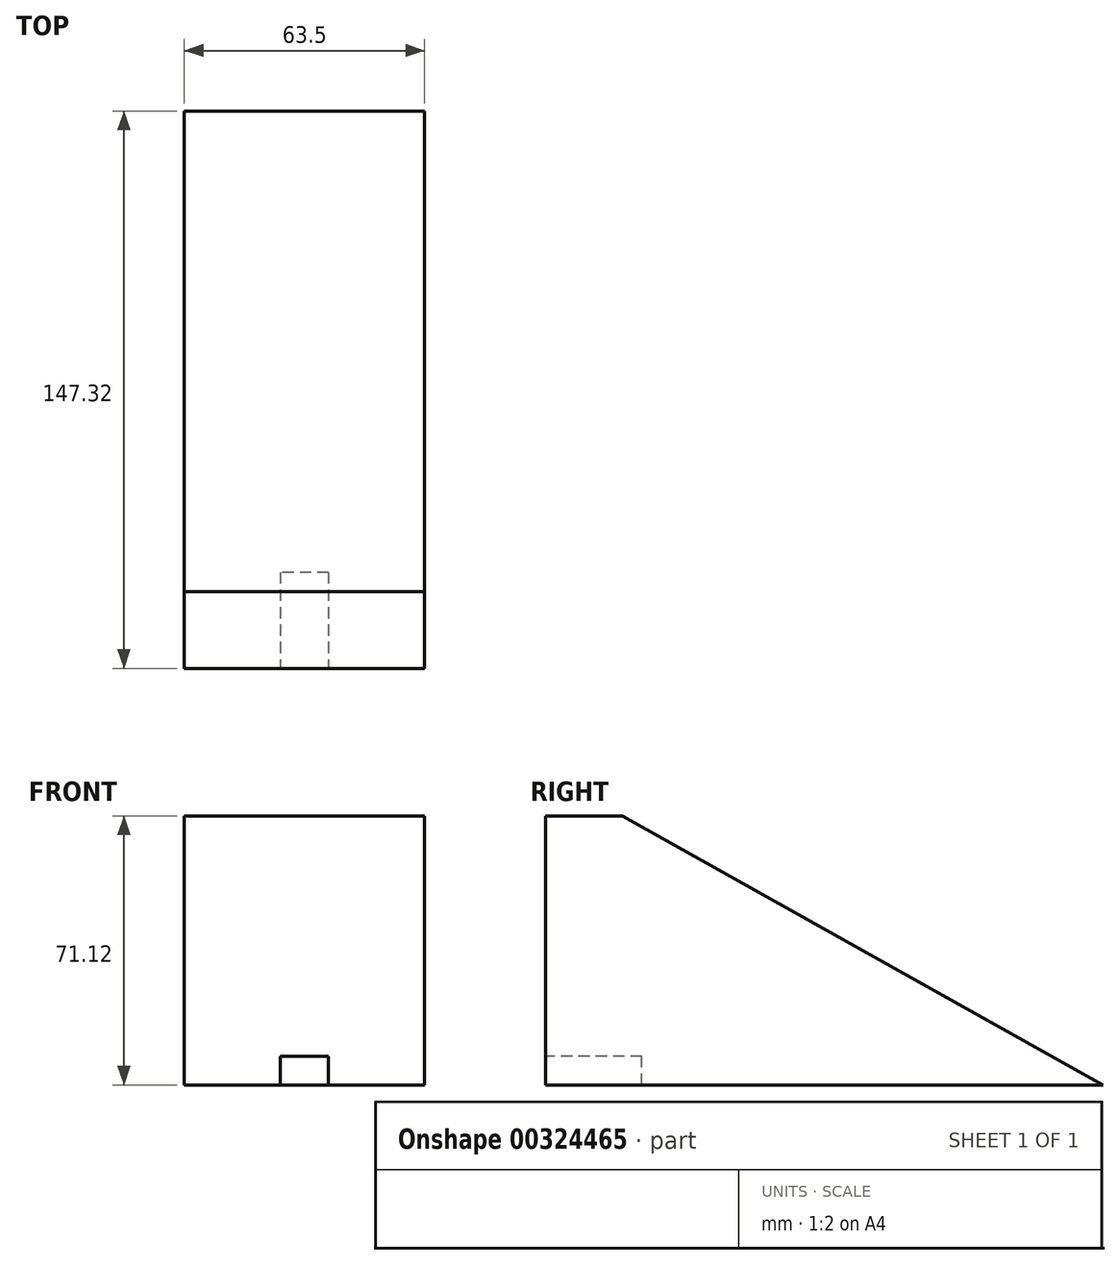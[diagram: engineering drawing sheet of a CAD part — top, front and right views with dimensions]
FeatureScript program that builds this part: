
annotation { "Feature Type Name" : "Feature", "Feature Type Description" : "" }
export const myFeature = defineFeature(function(context is Context, id is Id, definition is map)
    precondition{}
    {
        {
            var Q0;
            Q0=qCreatedBy(makeId("Right.planeOp"),FACE);
            var sketch = newSketch(context, id + "F0", { "sketchPlane" : qUnion([Q0])});
            skLineSegment(sketch, "E0", {"start": v(0, 0) * mm, "end": v(0, 71.12) * mm});
            skLineSegment(sketch, "E1", {"start": v(0, 71.12) * mm, "end": v(20.32, 71.12) * mm});
            skLineSegment(sketch, "E2", {"start": v(20.32, 71.12) * mm, "end": v(175.45, -15.75) * mm});
            skLineSegment(sketch, "E3", {"start": v(147.32, 0) * mm, "end": v(175.45, -15.75) * mm});
            skLineSegment(sketch, "E4", {"start": v(147.32, 0) * mm, "end": v(0, 0) * mm});
            skSolve(sketch);
        }
        {
            var Q0;
            Q0 = qSketchRegion(id + "F0", true);
            extrude(context, id + "F1", {"entities" : qUnion([Q0]), "depth" : 63.5 * mm});
        }
        {
            var Q0;
            Q0=qCreatedBy(makeId("Front.planeOp"),FACE);
            var sketch = newSketch(context, id + "F2", { "sketchPlane" : qUnion([Q0])});
            skLineSegment(sketch, "E5.bottom", {"start": v(38.1, 0) * mm, "end": v(25.4, 0) * mm});
            skLineSegment(sketch, "E5.top", {"start": v(38.1, 7.62) * mm, "end": v(25.4, 7.62) * mm});
            skLineSegment(sketch, "E5.left", {"start": v(38.1, 0) * mm, "end": v(38.1, 7.62) * mm});
            skLineSegment(sketch, "E5.right", {"start": v(25.4, 0) * mm, "end": v(25.4, 7.62) * mm});
            skSolve(sketch);
        }
        {
            var Q0;
            Q0 = qSketchRegion(id + "F2", true);
            extrude(context, id + "F3", {"entities" : qUnion([Q0]), "operationType" : NewBodyOperationType.REMOVE, "oppositeDirection" : true, "depth" : 25.4 * mm});
        }
    });
